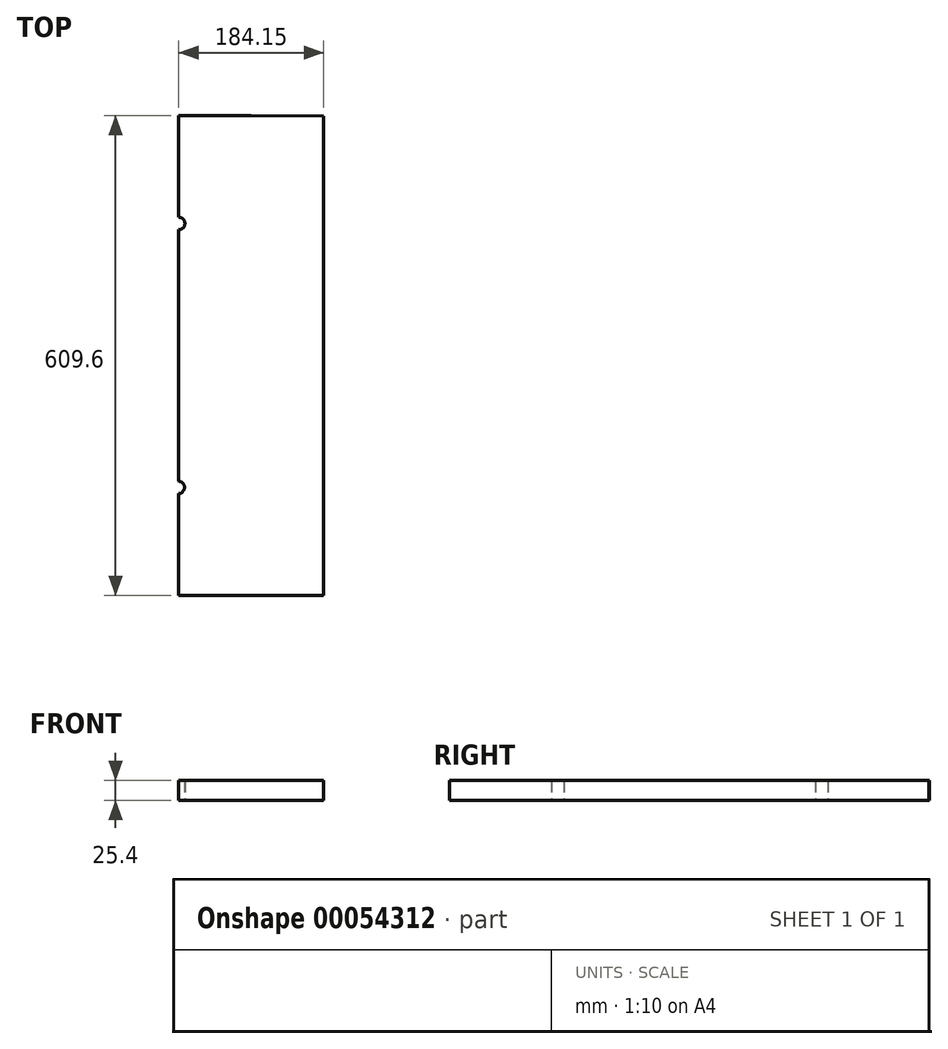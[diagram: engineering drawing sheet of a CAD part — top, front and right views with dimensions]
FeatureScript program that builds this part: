
annotation { "Feature Type Name" : "Feature", "Feature Type Description" : "" }
export const myFeature = defineFeature(function(context is Context, id is Id, definition is map)
    precondition{}
    {
        {
            var Q0;
            Q0=qCreatedBy(makeId("Top.planeOp"),FACE);
            var sketch = newSketch(context, id + "F0", { "sketchPlane" : qUnion([Q0])});
            skLineSegment(sketch, "E0", {"start": v(0, 0) * mm, "end": v(-184.15, 0) * mm});
            skLineSegment(sketch, "E1", {"start": v(-184.15, 0) * mm, "end": v(0, 0) * mm});
            skPoint(sketch, "E2.centerSnap0", {"position": v(-92.08, 609.6) * mm});
            skLineSegment(sketch, "E3", {"start": v(0, 0) * mm, "end": v(0, 518.16) * mm});
            skLineSegment(sketch, "E4", {"start": v(-184.15, 0) * mm, "end": v(-184.15, 518.16) * mm});
            skLineSegment(sketch, "E5", {"start": v(-92.07, 609.6) * mm, "end": v(0, 608.97) * mm});
            skLineSegment(sketch, "E6", {"start": v(0, 608.97) * mm, "end": v(0, 518.16) * mm});
            skLineSegment(sketch, "E7", {"start": v(-92.08, 609.6) * mm, "end": v(-184.15, 609.6) * mm});
            skLineSegment(sketch, "E8", {"start": v(-184.15, 609.6) * mm, "end": v(-184.15, 518.16) * mm});
            skLineSegment(sketch, "E9", {"start": v(-184.15, 609.6) * mm, "end": v(-184.15, 0) * mm});
            skLineSegment(sketch, "E10", {"start": v(0, 0) * mm, "end": v(0, 608.97) * mm});
            skLineSegment(sketch, "E11", {"start": v(-184.15, 609.6) * mm, "end": v(-184.15, 304.8) * mm});
            skLineSegment(sketch, "E12", {"start": v(-184.15, 304.8) * mm, "end": v(-184.15, 0) * mm});
            skLineSegment(sketch, "E13", {"start": v(-184.15, 152.4) * mm, "end": v(-184.15, 0) * mm});
            skLineSegment(sketch, "E14", {"start": v(-92.08, 0) * mm, "end": v(-92.08, 609.6) * mm});
            skLineSegment(sketch, "E15", {"start": v(0, 0) * mm, "end": v(0, 304.48) * mm});
            skLineSegment(sketch, "E16", {"start": v(0, 304.48) * mm, "end": v(0, 0) * mm});
            skLineSegment(sketch, "E17", {"start": v(0, 152.24) * mm, "end": v(0, 0) * mm});
            skLineSegment(sketch, "E18", {"start": v(0, 608.97) * mm, "end": v(0, 304.48) * mm});
            skLineSegment(sketch, "E19", {"start": v(0, 456.72) * mm, "end": v(0, 304.48) * mm});
            skLineSegment(sketch, "E20", {"start": v(-184.15, 457.2) * mm, "end": v(-184.15, 304.8) * mm});
            skLineSegment(sketch, "E21", {"start": v(-184.15, 518.16) * mm, "end": v(-184.15, 563.88) * mm});
            skPoint(sketch, "E22", {"position": v(0, 563.88) * mm});
            skCircle(sketch, "E23.MirrorC", {"center": v(-184.15, 472.43) * mm, "radius": 7.94 * mm});
            skCircle(sketch, "E24.MirrorC", {"center": v(-184.73, 137.17) * mm, "radius": 7.94 * mm});
            skSolve(sketch);
        }
        {
            var Q0;
            {var subQ2=sQuery(id+"F0.wireOp",EDGE,"E7");Q0=makeQuery(id+"F0.imprint","IMPRINT",FACE,{"disambiguationData":[TD([[makeQuery(id+"F0.imprint","IMPRINT",EDGE,{"derivedFrom":subQ2}),1.0]])]});}
            var Q1;
            {var subQ0=sQuery(id+"F0.wireOp",EDGE,"E5");Q1=makeQuery(id+"F0.imprint","IMPRINT",FACE,{"disambiguationData":[TD([[makeQuery(id+"F0.imprint","IMPRINT",EDGE,{"derivedFrom":subQ0}),-1.0]])]});}
            extrude(context, id + "F1", {"entities" : qUnion([Q0, Q1]), "depth" : 25.4 * mm});
        }
    });
